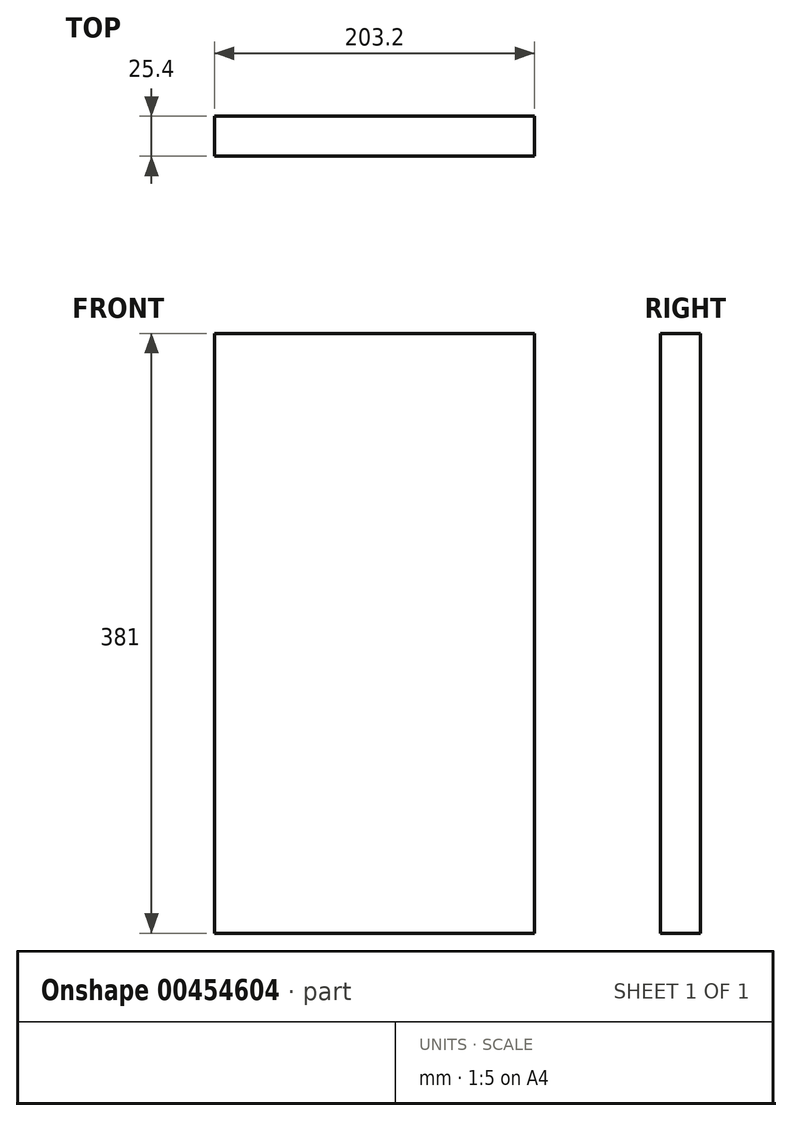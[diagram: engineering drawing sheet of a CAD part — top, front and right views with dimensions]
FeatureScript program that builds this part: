
annotation { "Feature Type Name" : "Feature", "Feature Type Description" : "" }
export const myFeature = defineFeature(function(context is Context, id is Id, definition is map)
    precondition{}
    {
        {
            var Q0;
            Q0=qCreatedBy(makeId("Top.planeOp"),FACE);
            var sketch = newSketch(context, id + "F0", { "sketchPlane" : qUnion([Q0])});
            skLineSegment(sketch, "E0.bottom", {"start": v(101.6, 12.7) * mm, "end": v(-101.6, 12.7) * mm});
            skLineSegment(sketch, "E0.top", {"start": v(101.6, -12.7) * mm, "end": v(-101.6, -12.7) * mm});
            skLineSegment(sketch, "E0.left", {"start": v(101.6, 12.7) * mm, "end": v(101.6, -12.7) * mm});
            skLineSegment(sketch, "E0.right", {"start": v(-101.6, 12.7) * mm, "end": v(-101.6, -12.7) * mm});
            skPoint(sketch, "E0.middle", {"position": v(0, 0) * mm});
            skSolve(sketch);
        }
        {
            var Q0;
            Q0=makeQuery(id+"F0.imprint","IMPRINT",FACE,{"disambiguationData":[TD([[makeQuery(id+"F0.imprint","IMPRINT",EDGE,{"derivedFrom":sQuery(id+"F0.wireOp",EDGE,"E0.bottom")}),1.0]])]});
            extrude(context, id + "F1", {"entities" : qUnion([Q0]), "depth" : 381 * mm});
        }
    });
